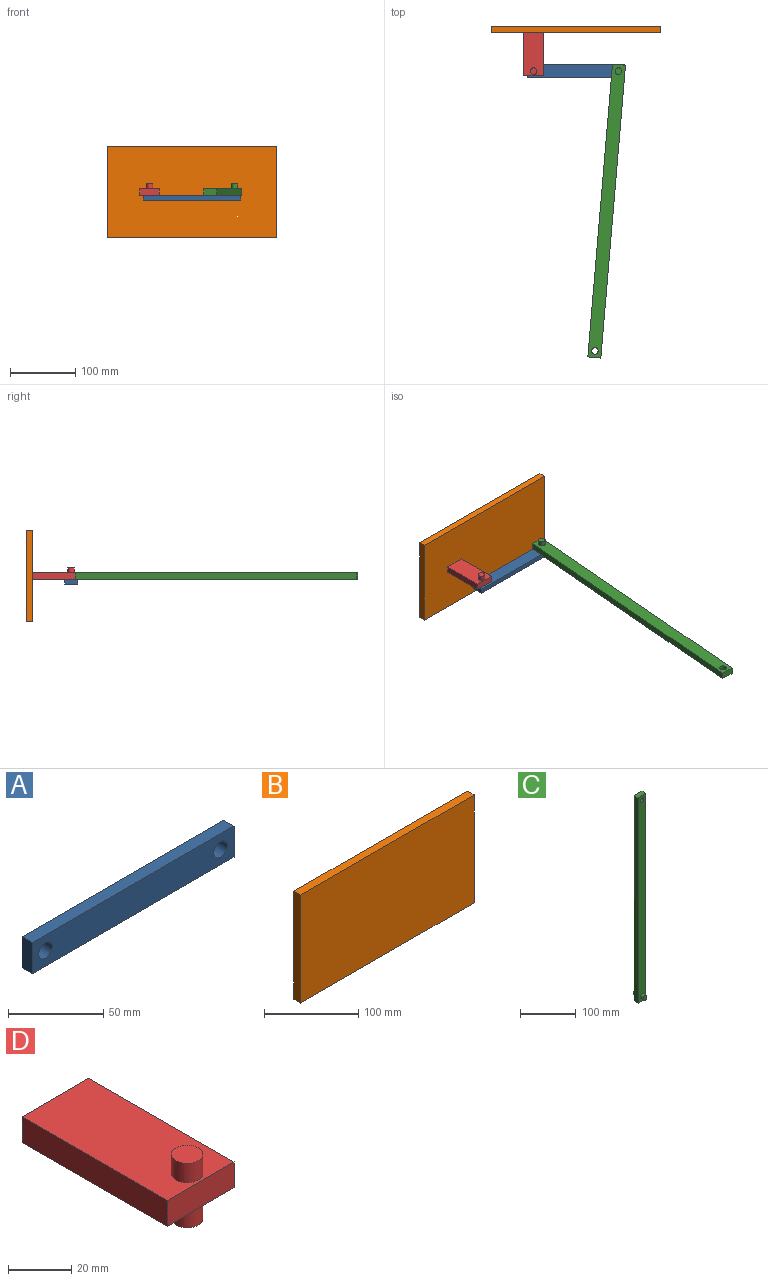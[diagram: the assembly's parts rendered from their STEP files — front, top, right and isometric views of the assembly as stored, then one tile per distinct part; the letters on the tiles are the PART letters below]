
ASSEMBLY  parts=4 mates=3
PART A: 8 faces, bbox 150x7.5x20 mm
  f0: plane 20x7.5mm, normal (-1,0,0), area 150mm2, adj f1,f5,f6,f7
  f1: plane 150x7.5mm, normal (0,0,-1), area 1125mm2, adj f0,f2,f6,f7
  f2: plane 20x7.5mm, normal (1,0,0), area 150mm2, adj f1,f5,f6,f7
  f3: cylinder r=5mm len=10mm, axis (0,1,0), area 235.6mm2, adj f6,f7
  f4: cylinder r=5mm len=10mm, axis (0,1,0), area 235.6mm2, adj f6,f7
  f5: plane 150x7.5mm, normal (0,0,1), area 1125mm2, adj f0,f2,f6,f7
  f6: plane 150x20mm, normal (0,-1,0), area 2842.9mm2, adj f0,f1,f2,f3,f4,f5
  f7: plane 150x20mm, normal (0,1,0), area 2842.9mm2, adj f0,f1,f2,f3,f4,f5
PART B: 6 faces, bbox 260x10x140 mm
  f0: plane 140x10mm, normal (-1,0,0), area 1400mm2, adj f1,f3,f4,f5
  f1: plane 260x10mm, normal (0,0,-1), area 2600mm2, adj f0,f2,f4,f5
  f2: plane 140x10mm, normal (1,0,0), area 1400mm2, adj f1,f3,f4,f5
  f3: plane 260x10mm, normal (0,0,1), area 2600mm2, adj f0,f2,f4,f5
  f4: plane 260x140mm, normal (0,-1,0), area 36400mm2, adj f0,f1,f2,f3
  f5: plane 260x140mm, normal (0,1,0), area 36400mm2, adj f0,f1,f2,f3
PART C: 11 faces, bbox 20x25x450 mm
  f0: plane 450x10mm, normal (1,0,0), area 4500mm2, adj f1,f4,f5,f6
  f1: plane 20x10mm, normal (0,0,1), area 200mm2, adj f0,f2,f5,f6
  f2: plane 450x10mm, normal (-1,0,0), area 4500mm2, adj f1,f4,f5,f6
  f3: cylinder r=5mm len=10mm, axis (0,1,0), area 314.2mm2, adj f5,f6
  f4: plane 20x10mm, normal (0,0,-1), area 200mm2, adj f0,f2,f5,f6
  f5: plane 450x20mm, normal (0,-1,0), area 8842.9mm2, adj f0,f1,f2,f3,f4,f9
  f6: plane 450x20mm, normal (0,1,0), area 8842.9mm2, adj f0,f1,f2,f3,f4,f8
  f7: plane 10x10mm, normal (0,1,0), area 78.5mm2, adj f8
  f8: cylinder r=5mm len=10mm, axis (0,1,0), area 235.6mm2, adj f6,f7
  f9: cylinder r=5mm len=10mm, axis (0,1,0), area 235.6mm2, adj f5,f10
  f10: plane 10x10mm, normal (0,-1,0), area 78.5mm2, adj f9
PART D: 10 faces, bbox 30x65x25 mm
  f0: plane 30x10mm, normal (0,1,0), area 300mm2, adj f1,f3,f4,f5
  f1: plane 65x10mm, normal (-1,0,0), area 650mm2, adj f0,f2,f4,f5
  f2: plane 30x10mm, normal (0,-1,0), area 300mm2, adj f1,f3,f4,f5
  f3: plane 65x10mm, normal (1,0,0), area 650mm2, adj f0,f2,f4,f5
  f4: plane 65x30mm, normal (0,0,1), area 1871.5mm2, adj f0,f1,f2,f3,f8
  f5: plane 65x30mm, normal (0,0,-1), area 1871.5mm2, adj f0,f1,f2,f3,f7
  f6: plane 10x10mm, normal (0,0,-1), area 78.5mm2, adj f7
  f7: cylinder r=5mm len=10mm, axis (0,0,-1), area 235.6mm2, adj f5,f6
  f8: cylinder r=5mm len=10mm, axis (0,0,-1), area 235.6mm2, adj f4,f9
  f9: plane 10x10mm, normal (0,0,1), area 78.5mm2, adj f8
PLACE A rot(axis=(1,0,0),90deg) t=(3.24,-41.87,-18.52)mm
PLACE B t=(3.24,22.13,-9.77)mm fixed
PLACE C rot(axis=(1,-0.04,-0.04),90.1deg) t=(83.24,-207.01,-9.77)mm
PLACE D rot(axis=(0,0,-1),0deg) t=(3.24,22.13,-9.77)mm
MATE revolute C.f8 <-> A.f4  axis (0,0,-1) through (68.24,-41.87,-22.27)mm
MATE fastened D.f0 <-> B.f4  axis (0,1,0) through (-61.76,17.13,-9.77)mm
MATE revolute A.f3 <-> D.f7  axis (0,0,-1) through (-61.76,-41.87,-22.27)mm
